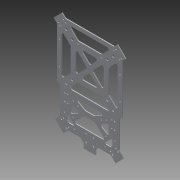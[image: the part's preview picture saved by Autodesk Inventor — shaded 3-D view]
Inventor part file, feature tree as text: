
AUTODESK INVENTOR PART (.ipt)
format: ipt  version: 2013 (Build 170138000, 138)  size: 12,797,952 bytes
history: native  units: mm
features: sketch x11, hole x6, extrude x5, other x2, fillet x2
ambient origin geometry x8: Origin, YZ Plane, XZ Plane, XY Plane, X Axis, Y Axis, Z Axis, Center Point
feature tree (26):
  other  "ソリッド1"
  extrude  "押し出し1"  Depth=115.0mm
  hole  "穴1"  [1 undecoded]
  hole  "穴2"  [1 undecoded]
  hole  "穴6"  [1 undecoded]
  hole  "穴7"  [1 undecoded]
  hole  "穴8"  [1 undecoded]
  extrude  "押し出し7"  TaperAngle=0.0deg  [1 undecoded]
  extrude  "押し出し8"  Depth=2.0mm TaperAngle=0.0deg
  extrude  "押し出し12"  Depth=3.2mm
  fillet  "フィレット1"  Radius=30.0mm
  extrude  "押し出し13"  Depth=8.0mm
  fillet  "フィレット2"  Radius=20.0mm
  hole  "穴9"  [1 undecoded]
  sketch  "スケッチ1"
  sketch  "スケッチ2"
  sketch  "スケッチ3"
  sketch  "スケッチ9"
  sketch  "スケッチ11"
  sketch  "スケッチ12"
  sketch  "スケッチ13"
  sketch  "スケッチ14"
  sketch  "スケッチ17"
  sketch  "スケッチ19"
  sketch  "スケッチ20"
  other  "断面エッジを投影1"
note: 7 required parameter values undecoded (feature->parameter linkage not recoverable at this tier; creation-order binding heuristic only, values carry confidence <= 0.55)
